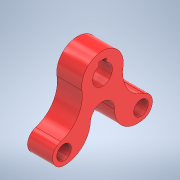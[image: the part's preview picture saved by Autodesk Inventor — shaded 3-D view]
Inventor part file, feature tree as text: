
AUTODESK INVENTOR PART (.ipt)
format: ipt  version: 2021 (Build 250183000, 183)  size: 174,592 bytes
history: native  units: in
note: dims shown in document units (in); Inventor stores cm internally (conversion verified against a paired STEP export)
features: sketch x3, extrude x1
ambient origin geometry x8: Origin, YZ Plane, XZ Plane, XY Plane, X Axis, Y Axis, Z Axis, Center Point
bodies: Solid1 (feature_tree)
feature tree (4):
  sketch  "Sketch1"  dims[d0=3.7402in d1=7.874in]
  sketch  "Sketch2"  dims[d2=0.689in]
  extrude  "Extrusion1"  Depth=7.874in
  sketch  "Sketch3"  dims[d3=1.378in d4=6.6929in d5=4.8819in d6=2.3622in d7=7.2835in d8=14.5669in d9=2.7559in d10=4.3307in d11=2.7559in d12=4.3307in d13=4.3307in d14=0.3937in d15=0.0in d16=0.0in d17=4.3307in d18=0.0344in d19=0.0197in d20=0.0344in]
